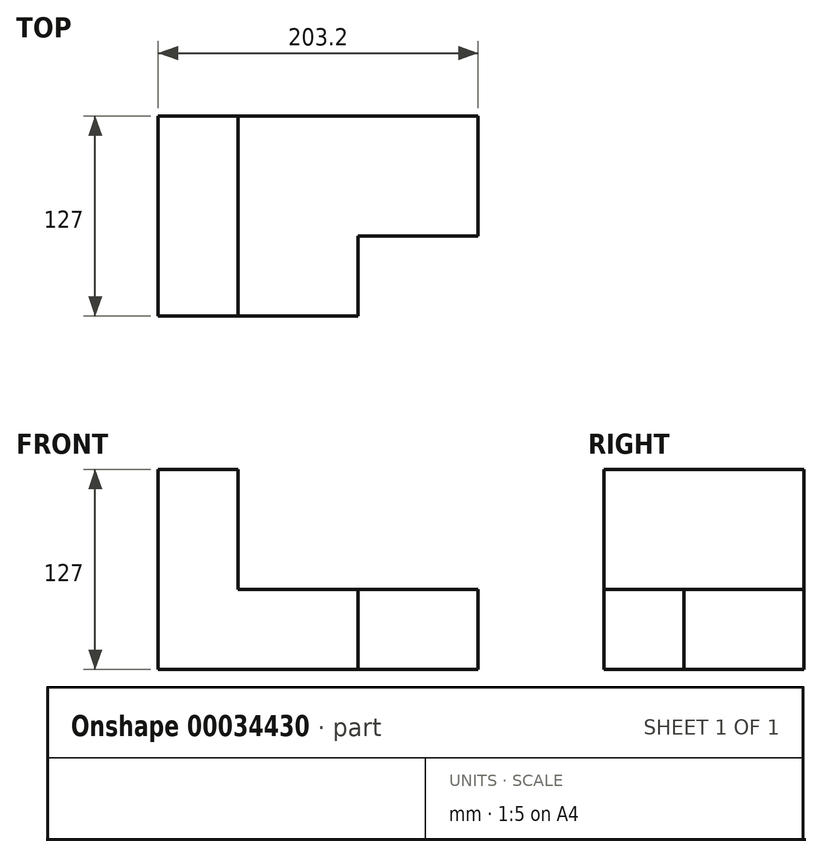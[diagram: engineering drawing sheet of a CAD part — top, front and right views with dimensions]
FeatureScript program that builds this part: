
annotation { "Feature Type Name" : "Feature", "Feature Type Description" : "" }
export const myFeature = defineFeature(function(context is Context, id is Id, definition is map)
    precondition{}
    {
        {
            var Q0;
            Q0=qCreatedBy(makeId("Top.planeOp"),FACE);
            var sketch = newSketch(context, id + "F0", { "sketchPlane" : qUnion([Q0])});
            skLineSegment(sketch, "E0.bottom", {"start": v(-34.04, 80.14) * mm, "end": v(169.16, 80.14) * mm});
            skLineSegment(sketch, "E0.top", {"start": v(-34.04, -46.86) * mm, "end": v(169.16, -46.86) * mm});
            skLineSegment(sketch, "E0.left", {"start": v(-34.04, 80.14) * mm, "end": v(-34.04, -46.86) * mm});
            skLineSegment(sketch, "E0.right", {"start": v(169.16, 80.14) * mm, "end": v(169.16, -46.86) * mm});
            skSolve(sketch);
        }
        {
            var Q0;
            Q0=makeQuery(id+"F0.imprint","IMPRINT",FACE,{"disambiguationData":[TD([[makeQuery(id+"F0.imprint","IMPRINT",EDGE,{"derivedFrom":sQuery(id+"F0.wireOp",EDGE,"E0.bottom")}),-1.0]])]});
            extrude(context, id + "F1", {"entities" : qUnion([Q0]), "depth" : 127 * mm});
        }
        {
            var Q0;
            Q0=makeQuery(id+"F1.opExtrude","CAP_FACE",FACE,{"disambiguationData":[OSD([sQuery(id+"F0.wireOp",EDGE,"E0.bottom"),sQuery(id+"F0.wireOp",EDGE,"E0.top"),sQuery(id+"F0.wireOp",EDGE,"E0.left"),sQuery(id+"F0.wireOp",EDGE,"E0.right")])],"isStart":false});
            var sketch = newSketch(context, id + "F2", { "sketchPlane" : qUnion([Q0])});
            skLineSegment(sketch, "E1.bottom", {"start": v(169.16, -46.86) * mm, "end": v(16.76, -46.86) * mm});
            skLineSegment(sketch, "E1.top", {"start": v(169.16, 80.14) * mm, "end": v(16.76, 80.14) * mm});
            skLineSegment(sketch, "E1.left", {"start": v(169.16, -46.86) * mm, "end": v(169.16, 80.14) * mm});
            skLineSegment(sketch, "E1.right", {"start": v(16.76, -46.86) * mm, "end": v(16.76, 80.14) * mm});
            skSolve(sketch);
        }
        {
            var Q0;
            Q0=makeQuery(id+"F2.imprint","IMPRINT",FACE,{"disambiguationData":[TD([[makeQuery(id+"F2.imprint","IMPRINT",EDGE,{"derivedFrom":sQuery(id+"F2.wireOp",EDGE,"E1.bottom")}),1.0]])]});
            extrude(context, id + "F3", {"entities" : qUnion([Q0]), "operationType" : NewBodyOperationType.REMOVE, "oppositeDirection" : true, "depth" : 76.2 * mm});
        }
        {
            var Q0;
            Q0=makeQuery(id+"F3.boolean.opBoolean","COPY",FACE,{"derivedFrom":makeQuery(id+"F3.opExtrude","CAP_FACE",FACE,{"disambiguationData":[OSD([sQuery(id+"F2.wireOp",EDGE,"E1.bottom"),sQuery(id+"F2.wireOp",EDGE,"E1.top"),sQuery(id+"F2.wireOp",EDGE,"E1.left"),sQuery(id+"F2.wireOp",EDGE,"E1.right")])],"isStart":false})});
            var sketch = newSketch(context, id + "F4", { "sketchPlane" : qUnion([Q0])});
            skLineSegment(sketch, "E2.bottom", {"start": v(169.16, -46.86) * mm, "end": v(92.96, -46.86) * mm});
            skLineSegment(sketch, "E2.top", {"start": v(169.16, 3.94) * mm, "end": v(92.96, 3.94) * mm});
            skLineSegment(sketch, "E2.left", {"start": v(169.16, -46.86) * mm, "end": v(169.16, 3.94) * mm});
            skLineSegment(sketch, "E2.right", {"start": v(92.96, -46.86) * mm, "end": v(92.96, 3.94) * mm});
            skSolve(sketch);
        }
        {
            var Q0;
            Q0 = qSketchRegion(id + "F4", true);
            extrude(context, id + "F5", {"entities" : qUnion([Q0]), "operationType" : NewBodyOperationType.REMOVE, "oppositeDirection" : true, "depth" : 50.8 * mm});
        }
    });
